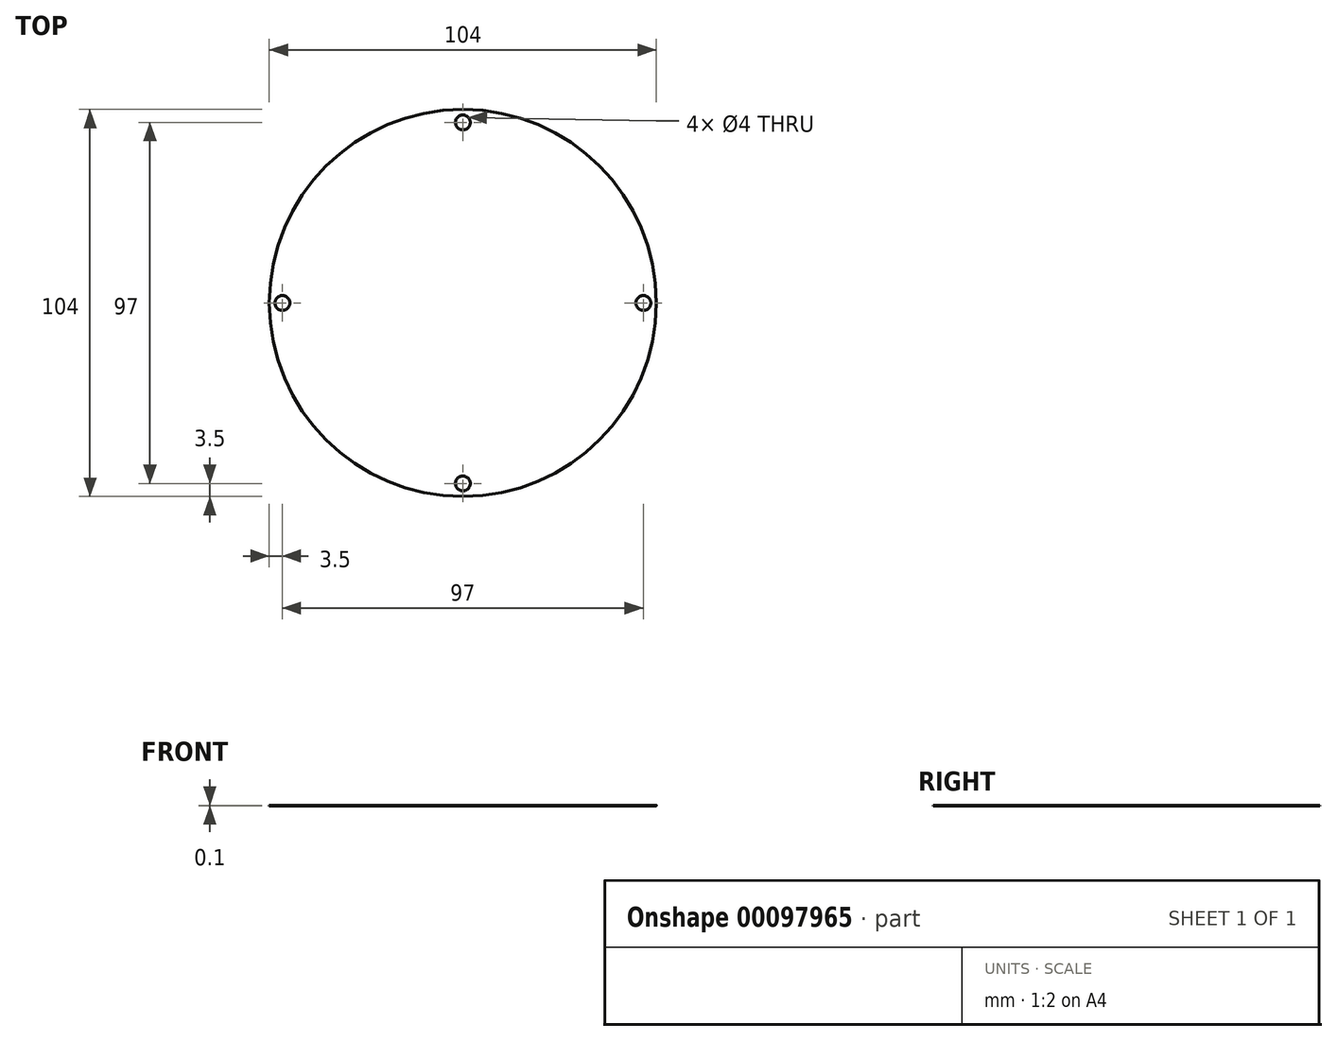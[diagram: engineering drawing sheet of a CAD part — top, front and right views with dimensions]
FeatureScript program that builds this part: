
annotation { "Feature Type Name" : "Feature", "Feature Type Description" : "" }
export const myFeature = defineFeature(function(context is Context, id is Id, definition is map)
    precondition{}
    {
        {
            var Q0;
            Q0=qCreatedBy(makeId("Top.planeOp"),FACE);
            var sketch = newSketch(context, id + "F0", { "sketchPlane" : qUnion([Q0])});
            skCircle(sketch, "E0", {"center": v(0, 0) * mm, "radius": 52 * mm});
            skSolve(sketch);
        }
        {
            var Q0;
            Q0 = qSketchRegion(id + "F0", true);
            extrude(context, id + "F1", {"entities" : qUnion([Q0]), "depth" : 0.1 * mm});
        }
        {
            var Q0;
            Q0=qCreatedBy(makeId("Top.planeOp"),FACE);
            var sketch = newSketch(context, id + "F2", { "sketchPlane" : qUnion([Q0])});
            skCircle(sketch, "E1", {"center": v(0, 0) * mm, "radius": 48.5 * mm, "construction": true});
            skCircle(sketch, "E2", {"center": v(48.5, 0) * mm, "radius": 2 * mm});
            skCircle(sketch, "E3", {"center": v(0, 48.5) * mm, "radius": 2 * mm});
            skCircle(sketch, "E4", {"center": v(-48.5, 0) * mm, "radius": 2 * mm});
            skCircle(sketch, "E5", {"center": v(0, -48.5) * mm, "radius": 2 * mm});
            skSolve(sketch);
        }
        {
            var Q0;
            Q0 = qSketchRegion(id + "F2", true);
            extrude(context, id + "F3", {"entities" : qUnion([Q0]), "operationType" : NewBodyOperationType.REMOVE, "endBound" : BoundingType.THROUGH_ALL, "depth" : 25 * mm});
        }
    });
